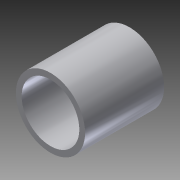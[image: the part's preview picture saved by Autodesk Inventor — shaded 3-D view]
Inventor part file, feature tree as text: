
AUTODESK INVENTOR PART (.ipt)
format: ipt  version: 2014 SP1 (Build 180222100, 222)  size: 86,016 bytes
history: native  units: in
note: dims shown in document units (in); Inventor stores cm internally (conversion verified against a paired STEP export)
features: extrude x1, sketch x1
ambient origin geometry x8: Origin, YZ Plane, XZ Plane, XY Plane, X Axis, Y Axis, Z Axis, Center Point
bodies: Solid1 (feature_tree)
feature tree (2):
  extrude  "Extrusion1"  Depth=0.8568in
  sketch  "Sketch1"  dims[d0=0.75in d1=0.625in d2=0.8568in d3=0.0in]
